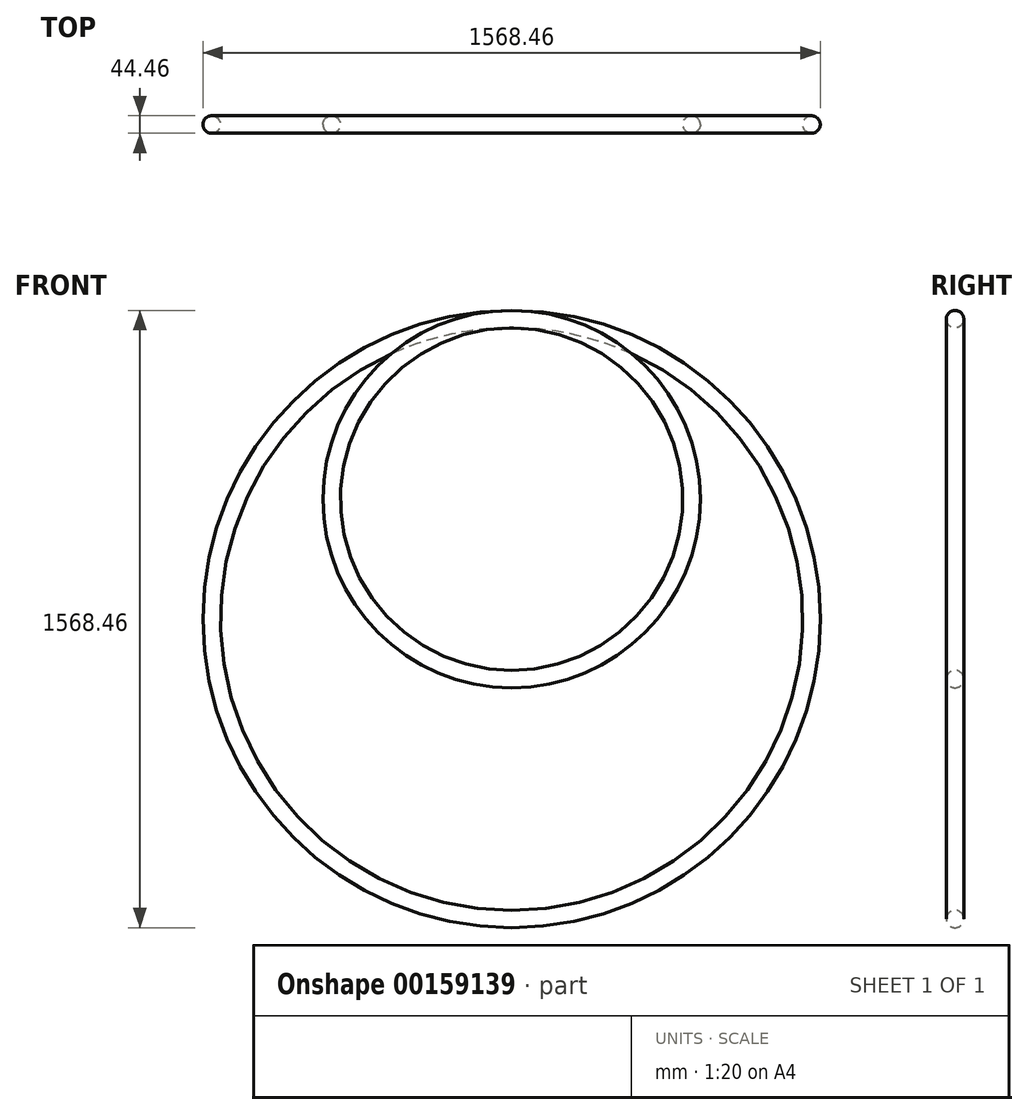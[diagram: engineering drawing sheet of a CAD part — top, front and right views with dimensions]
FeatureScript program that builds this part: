
annotation { "Feature Type Name" : "Feature", "Feature Type Description" : "" }
export const myFeature = defineFeature(function(context is Context, id is Id, definition is map)
    precondition{}
    {
        {
            var Q0;
            Q0=qCreatedBy(makeId("Right.planeOp"),FACE);
            var sketch = newSketch(context, id + "F0", { "sketchPlane" : qUnion([Q0])});
            skCircle(sketch, "E0", {"center": v(0, 0) * mm, "radius": 22.23 * mm});
            skSolve(sketch);
        }
        {
            var Q0;
            Q0=qCreatedBy(makeId("Front.planeOp"),FACE);
            var sketch = newSketch(context, id + "F1", { "sketchPlane" : qUnion([Q0])});
            skCircle(sketch, "E1", {"center": v(0, -762) * mm, "radius": 762 * mm});
            skSolve(sketch);
        }
        {
            var Q0;
            Q0=makeQuery(id+"F0.imprint","IMPRINT",FACE,{"disambiguationData":[TD([[makeQuery(id+"F0.imprint","IMPRINT",EDGE,{"derivedFrom":sQuery(id+"F0.wireOp",EDGE,"E0")}),1.0]])]});
            var Q1;
            Q1=sQuery(id+"F1.wireOp",EDGE,"E1");
            sweep(context, id + "F2", {"profiles" : qUnion([Q0]), "path" : qUnion([Q1])});
        }
        {
            var Q0;
            Q0=qCreatedBy(makeId("Right.planeOp"),FACE);
            var sketch = newSketch(context, id + "F3", { "sketchPlane" : qUnion([Q0])});
            skCircle(sketch, "E2", {"center": v(0, 0) * mm, "radius": 22.23 * mm});
            skSolve(sketch);
        }
        {
            var Q0;
            Q0=qCreatedBy(makeId("Front.planeOp"),FACE);
            var sketch = newSketch(context, id + "F4", { "sketchPlane" : qUnion([Q0])});
            skCircle(sketch, "E3", {"center": v(0, -457.2) * mm, "radius": 457.2 * mm});
            skSolve(sketch);
        }
        {
            var Q0;
            Q0=makeQuery(id+"F3.imprint","IMPRINT",FACE,{"disambiguationData":[TD([[makeQuery(id+"F3.imprint","IMPRINT",EDGE,{"derivedFrom":sQuery(id+"F3.wireOp",EDGE,"E2")}),1.0]])]});
            var Q1;
            Q1=sQuery(id+"F4.wireOp",EDGE,"E3");
            sweep(context, id + "F5", {"profiles" : qUnion([Q0]), "path" : qUnion([Q1])});
        }
    });
